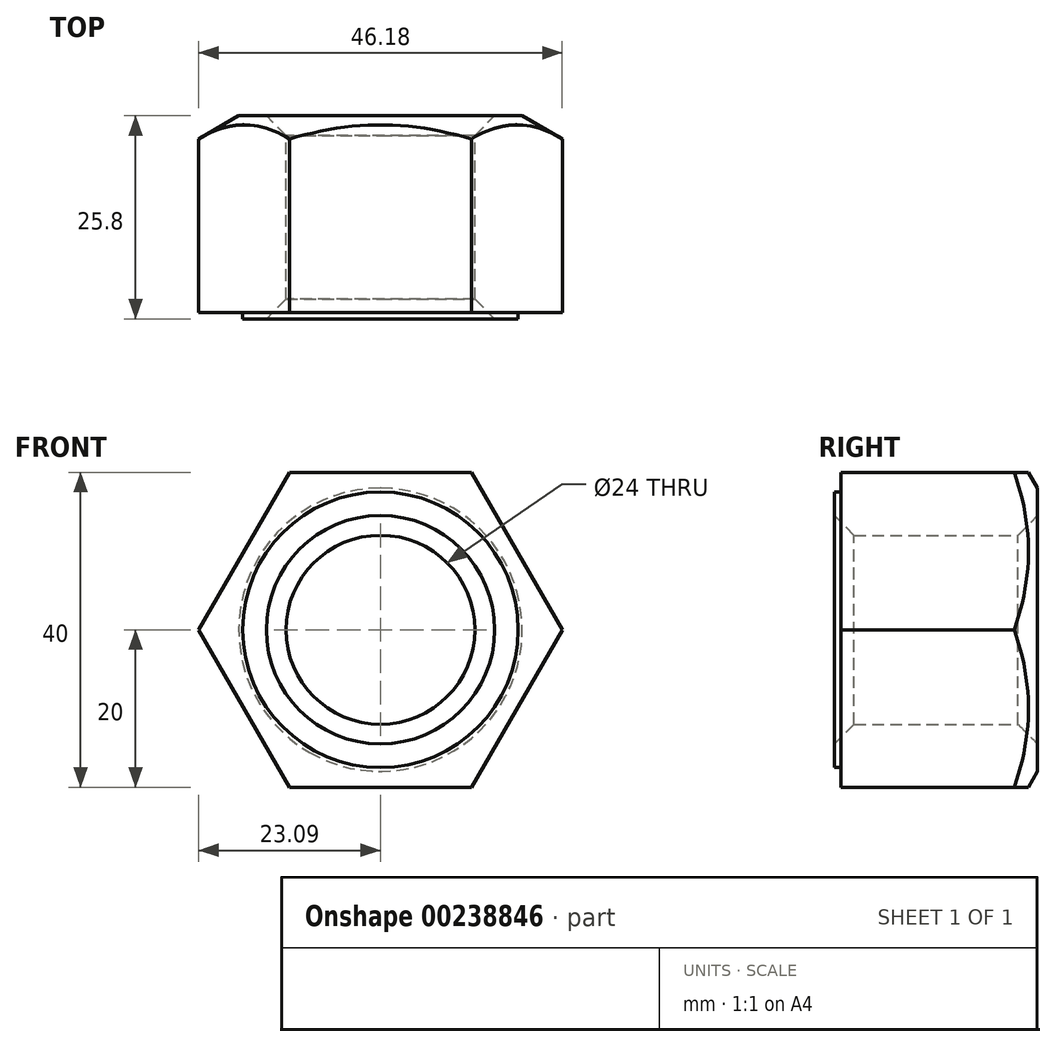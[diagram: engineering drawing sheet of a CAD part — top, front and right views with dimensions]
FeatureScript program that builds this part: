
annotation { "Feature Type Name" : "Feature", "Feature Type Description" : "" }
export const myFeature = defineFeature(function(context is Context, id is Id, definition is map)
    precondition{}
    {
        {
            var Q0;
            Q0=qCreatedBy(makeId("Front.planeOp"),FACE);
            var sketch = newSketch(context, id + "F0", { "sketchPlane" : qUnion([Q0])});
            skCircle(sketch, "E0.cCircle", {"center": v(0, 0) * mm, "radius": 20 * mm, "construction": true});
            skLineSegment(sketch, "E0.0", {"start": v(23.1, 0) * mm, "end": v(11.55, -20) * mm});
            skLineSegment(sketch, "E0.1", {"start": v(11.55, -20) * mm, "end": v(-11.55, -20) * mm});
            skLineSegment(sketch, "E0.2", {"start": v(-11.55, -20) * mm, "end": v(-23.1, 0) * mm});
            skLineSegment(sketch, "E0.3", {"start": v(-23.1, 0) * mm, "end": v(-11.55, 20) * mm});
            skLineSegment(sketch, "E0.4", {"start": v(-11.55, 20) * mm, "end": v(11.55, 20) * mm});
            skLineSegment(sketch, "E0.5", {"start": v(11.55, 20) * mm, "end": v(23.1, 0) * mm});
            skPoint(sketch, "E0.0.midPoint", {"position": v(17.32, -10) * mm});
            skCircle(sketch, "E1", {"center": v(0, 0) * mm, "radius": 12 * mm});
            skSolve(sketch);
        }
        {
            var Q0;
            Q0 = qSketchRegion(id + "F0", true);
            extrude(context, id + "F1", {"entities" : qUnion([Q0]), "depth" : 25 * mm});
        }
        {
            var Q0;
            Q0=qCreatedBy(makeId("Top.planeOp"),FACE);
            var sketch = newSketch(context, id + "F2", { "sketchPlane" : qUnion([Q0])});
            skLineSegment(sketch, "E2", {"start": v(0, -69.01) * mm, "end": v(0, 50.37) * mm, "construction": true});
            skLineSegment(sketch, "E3", {"start": v(18, 0) * mm, "end": v(34.06, -9.27) * mm});
            skLineSegment(sketch, "E4", {"start": v(34.06, -9.27) * mm, "end": v(31.62, 2.6) * mm});
            skLineSegment(sketch, "E5", {"start": v(31.62, 2.6) * mm, "end": v(18, 0) * mm});
            skSolve(sketch);
        }
        {
            var Q0;
            Q0 = qSketchRegion(id + "F2", true);
            var Q1;
            Q1=sQuery(id+"F2.wireOp",EDGE,"E2");
            revolve(context, id + "F3", {"operationType" : NewBodyOperationType.REMOVE, "entities" : qUnion([Q0]), "axis" : qUnion([Q1]), "revolveType" : RevolveType.FULL, "oppositeDirection" : true});
        }
        {
            var Q0;
            Q0=makeQuery(id+"F1.opExtrude","CAP_FACE",FACE,{"disambiguationData":[OSD([sQuery(id+"F0.wireOp",EDGE,"E0.0"),sQuery(id+"F0.wireOp",EDGE,"E0.1"),sQuery(id+"F0.wireOp",EDGE,"E0.2"),sQuery(id+"F0.wireOp",EDGE,"E0.3"),sQuery(id+"F0.wireOp",EDGE,"E0.4"),sQuery(id+"F0.wireOp",EDGE,"E0.5"),sQuery(id+"F0.wireOp",EDGE,"E1")])],"isStart":false});
            var sketch = newSketch(context, id + "F4", { "sketchPlane" : qUnion([Q0])});
            skCircle(sketch, "E6", {"center": v(0, 0) * mm, "radius": 17.5 * mm});
            skCircle(sketch, "E7", {"center": v(0, 0) * mm, "radius": 12 * mm});
            skSolve(sketch);
        }
        {
            var Q0;
            Q0=makeQuery(id+"F4.imprint","IMPRINT",FACE,{"disambiguationData":[TD([[makeQuery(id+"F4.imprint","IMPRINT",EDGE,{"derivedFrom":sQuery(id+"F4.wireOp",EDGE,"E6")}),1.0]])]});
            extrude(context, id + "F5", {"entities" : qUnion([Q0]), "operationType" : NewBodyOperationType.ADD, "depth" : 0.8 * mm});
        }
        {
            var Q0;
            Q0=makeQuery(id+"F5.opExtrude","CAP_EDGE",EDGE,{"disambiguationData":[OSD([sQuery(id+"F4.wireOp",EDGE,"E7")])],"isStart":false});
            var Q1;
            Q1=makeQuery(id+"F1.opExtrude","CAP_EDGE",EDGE,{"disambiguationData":[OSD([sQuery(id+"F0.wireOp",EDGE,"E1")])],"isStart":true});
            chamfer(context, id + "F6", {"entities" : qUnion([Q0, Q1]), "width" : 2.5 * mm, "tangentPropagation" : true});
        }
    });
